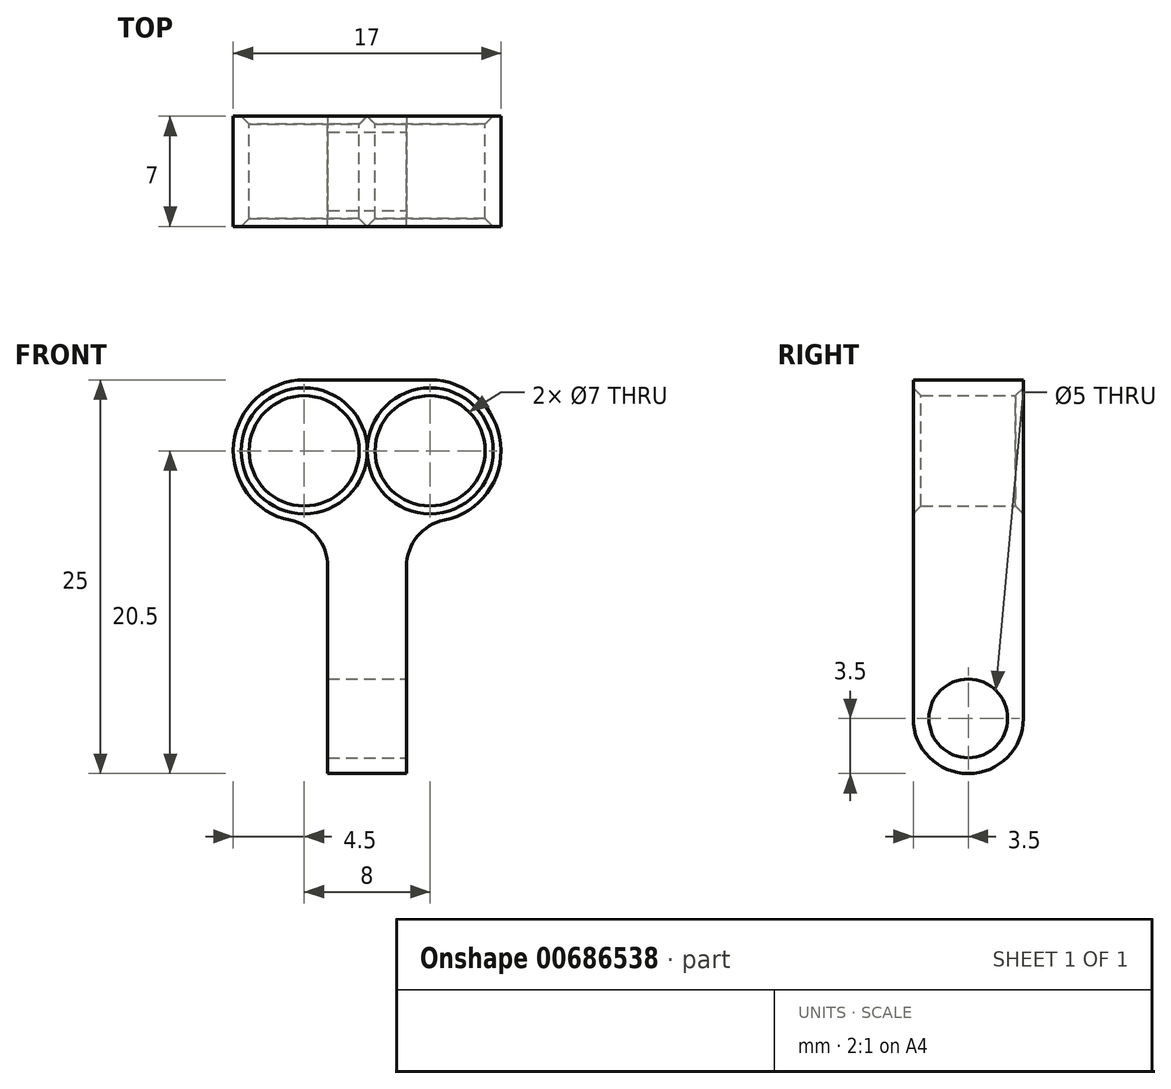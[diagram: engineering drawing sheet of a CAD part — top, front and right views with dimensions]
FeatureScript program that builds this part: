
annotation { "Feature Type Name" : "Feature", "Feature Type Description" : "" }
export const myFeature = defineFeature(function(context is Context, id is Id, definition is map)
    precondition{}
    {
        {
            var Q0;
            Q0=qCreatedBy(makeId("Front.planeOp"),FACE);
            var sketch = newSketch(context, id + "F0", { "sketchPlane" : qUnion([Q0])});
            skLineSegment(sketch, "E0.bottom", {"start": v(2.5, 12.5) * mm, "end": v(-2.5, 12.5) * mm});
            skLineSegment(sketch, "E0.top", {"start": v(2.5, -12.5) * mm, "end": v(-2.5, -12.5) * mm});
            skLineSegment(sketch, "E0.left", {"start": v(2.5, 12.5) * mm, "end": v(2.5, -12.5) * mm});
            skLineSegment(sketch, "E0.right", {"start": v(-2.5, 12.5) * mm, "end": v(-2.5, -12.5) * mm});
            skPoint(sketch, "E0.middle", {"position": v(0, 0) * mm});
            skLineSegment(sketch, "E1.bottom", {"start": v(-8.5, 12.5) * mm, "end": v(8.5, 12.5) * mm});
            skLineSegment(sketch, "E1.top", {"start": v(-8.5, 3.5) * mm, "end": v(8.5, 3.5) * mm});
            skLineSegment(sketch, "E1.left", {"start": v(-8.5, 12.5) * mm, "end": v(-8.5, 3.5) * mm});
            skLineSegment(sketch, "E1.right", {"start": v(8.5, 12.5) * mm, "end": v(8.5, 3.5) * mm});
            skCircle(sketch, "E2", {"center": v(-4, 8) * mm, "radius": 3.5 * mm});
            skCircle(sketch, "E3", {"center": v(4, 8) * mm, "radius": 3.5 * mm});
            skSolve(sketch);
        }
        {
            var Q0;
            {var subQ0=sQuery(id+"F0.wireOp",EDGE,"E1.right");Q0=makeQuery(id+"F0.imprint","IMPRINT",FACE,{"disambiguationData":[TD([[makeQuery(id+"F0.imprint","IMPRINT",EDGE,{"derivedFrom":subQ0}),-1.0]])]});}
            var Q1;
            {var subQ3=sQuery(id+"F0.wireOp",EDGE,"E1.left");Q1=makeQuery(id+"F0.imprint","IMPRINT",FACE,{"disambiguationData":[TD([[makeQuery(id+"F0.imprint","IMPRINT",EDGE,{"derivedFrom":subQ3}),1.0]])]});}
            var Q2;
            {var subQ6=sQuery(id+"F0.wireOp",EDGE,"E1.bottom");var subQ8=sQuery(id+"F0.wireOp",EDGE,"E0.left");var subQ12=makeQuery(id+"F0.imprint","INTERSECT",VERTEX,{"derivedFrom":[subQ8,subQ6]});Q2=makeQuery(id+"F0.imprint","IMPRINT",FACE,{"disambiguationData":[TD([[makeQuery(id+"F0.imprint","IMPRINT",EDGE,{"disambiguationData":[TD([[subQ12,-1.0]])],"derivedFrom":subQ8}),-1.0]])]});}
            var Q3;
            {var subQ0=sQuery(id+"F0.wireOp",EDGE,"E0.top");Q3=makeQuery(id+"F0.imprint","IMPRINT",FACE,{"disambiguationData":[TD([[makeQuery(id+"F0.imprint","IMPRINT",EDGE,{"derivedFrom":subQ0}),-1.0]])]});}
            extrude(context, id + "F1", {"entities" : qUnion([Q0, Q1, Q2, Q3]), "depth" : 7 * mm, "offsetDistance" : 25 * mm});
        }
        {
            var Q0;
            Q0=makeQuery(id+"F1.opExtrude","SWEPT_FACE",FACE,{"disambiguationData":[OSD([sQuery(id+"F0.wireOp",EDGE,"E0.left")])]});
            var sketch = newSketch(context, id + "F2", { "sketchPlane" : qUnion([Q0])});
            skCircle(sketch, "E4", {"center": v(-3.5, -9) * mm, "radius": 2.5 * mm});
            skSolve(sketch);
        }
        {
            var Q0;
            Q0=sQuery(id+"F2.wireOp",VERTEX,"E4.center");
            var Q1;
            Q1=makeQuery(id+"F1.opExtrude","SWEPT_BODY",BODY,{"disambiguationData":[OSD([sQuery(id+"F0.wireOp",EDGE,"E0.top"),sQuery(id+"F0.wireOp",EDGE,"E0.left"),sQuery(id+"F0.wireOp",EDGE,"E0.right"),sQuery(id+"F0.wireOp",EDGE,"E1.bottom"),sQuery(id+"F0.wireOp",EDGE,"E1.top"),sQuery(id+"F0.wireOp",EDGE,"E1.left"),sQuery(id+"F0.wireOp",EDGE,"E1.right"),sQuery(id+"F0.wireOp",EDGE,"E2"),sQuery(id+"F0.wireOp",EDGE,"E3")])]});
            hole(context, id + "F3", {"style" : HoleStyle.SIMPLE, "endStyle" : HoleEndStyle.THROUGH, "holeDiameter" : 5 * mm, "majorDiameter" : 5 * mm, "isTappedThrough" : true, "tappedDepth" : 12 * mm, "tapClearance" : 3, "startFromSketch" : true, "locations" : qUnion([Q0]), "scope" : qUnion([Q1])});
        }
        {
            var Q0;
            Q0=makeQuery(id+"F1.opExtrude","SWEPT_EDGE",EDGE,{"disambiguationData":[OSD([sQuery(id+"F0.wireOp",EDGE,"E1.bottom"),sQuery(id+"F0.wireOp",EDGE,"E1.right")])]});
            var Q1;
            Q1=makeQuery(id+"F1.opExtrude","SWEPT_EDGE",EDGE,{"disambiguationData":[OSD([sQuery(id+"F0.wireOp",EDGE,"E1.bottom"),sQuery(id+"F0.wireOp",EDGE,"E1.left")])]});
            var Q2;
            Q2=makeQuery(id+"F1.opExtrude","SWEPT_EDGE",EDGE,{"disambiguationData":[OSD([sQuery(id+"F0.wireOp",EDGE,"E1.top"),sQuery(id+"F0.wireOp",EDGE,"E1.right")])]});
            var Q3;
            Q3=makeQuery(id+"F1.opExtrude","SWEPT_EDGE",EDGE,{"disambiguationData":[OSD([sQuery(id+"F0.wireOp",EDGE,"E1.top"),sQuery(id+"F0.wireOp",EDGE,"E1.left")])]});
            fillet(context, id + "F4", {"entities" : qUnion([Q0, Q1, Q2, Q3]), "radius" : 4.5 * mm, "tangentPropagation" : true, "allowEdgeOverflow" : false});
        }
        {
            var Q0;
            Q0=makeQuery(id+"F1.opExtrude","CAP_EDGE",EDGE,{"disambiguationData":[OSD([sQuery(id+"F0.wireOp",EDGE,"E0.top")])],"isStart":true});
            var Q1;
            Q1=makeQuery(id+"F1.opExtrude","CAP_EDGE",EDGE,{"disambiguationData":[OSD([sQuery(id+"F0.wireOp",EDGE,"E0.top")])],"isStart":false});
            fillet(context, id + "F5", {"entities" : qUnion([Q0, Q1]), "radius" : 3.5 * mm, "tangentPropagation" : true, "allowEdgeOverflow" : false});
        }
        {
            var Q0;
            Q0=makeQuery(id+"F1.opExtrude","SWEPT_EDGE",EDGE,{"disambiguationData":[OSD([sQuery(id+"F0.wireOp",EDGE,"E0.left"),sQuery(id+"F0.wireOp",EDGE,"E1.top")])]});
            var Q1;
            Q1=makeQuery(id+"F1.opExtrude","SWEPT_EDGE",EDGE,{"disambiguationData":[OSD([sQuery(id+"F0.wireOp",EDGE,"E0.right"),sQuery(id+"F0.wireOp",EDGE,"E1.top")])]});
            fillet(context, id + "F6", {"entities" : qUnion([Q0, Q1]), "radius" : 3 * mm, "tangentPropagation" : true, "allowEdgeOverflow" : false});
        }
        {
            var Q0;
            Q0=makeQuery(id+"F1.opExtrude","CAP_EDGE",EDGE,{"disambiguationData":[OSD([sQuery(id+"F0.wireOp",EDGE,"E2")])],"isStart":false});
            var Q1;
            Q1=makeQuery(id+"F1.opExtrude","CAP_EDGE",EDGE,{"disambiguationData":[OSD([sQuery(id+"F0.wireOp",EDGE,"E3")])],"isStart":false});
            var Q2;
            Q2=makeQuery(id+"F1.opExtrude","CAP_EDGE",EDGE,{"disambiguationData":[OSD([sQuery(id+"F0.wireOp",EDGE,"E2")])],"isStart":true});
            var Q3;
            Q3=makeQuery(id+"F1.opExtrude","CAP_EDGE",EDGE,{"disambiguationData":[OSD([sQuery(id+"F0.wireOp",EDGE,"E3")])],"isStart":true});
            chamfer(context, id + "F7", {"entities" : qUnion([Q0, Q1, Q2, Q3]), "width" : 0.5 * mm, "tangentPropagation" : true});
        }
    });
